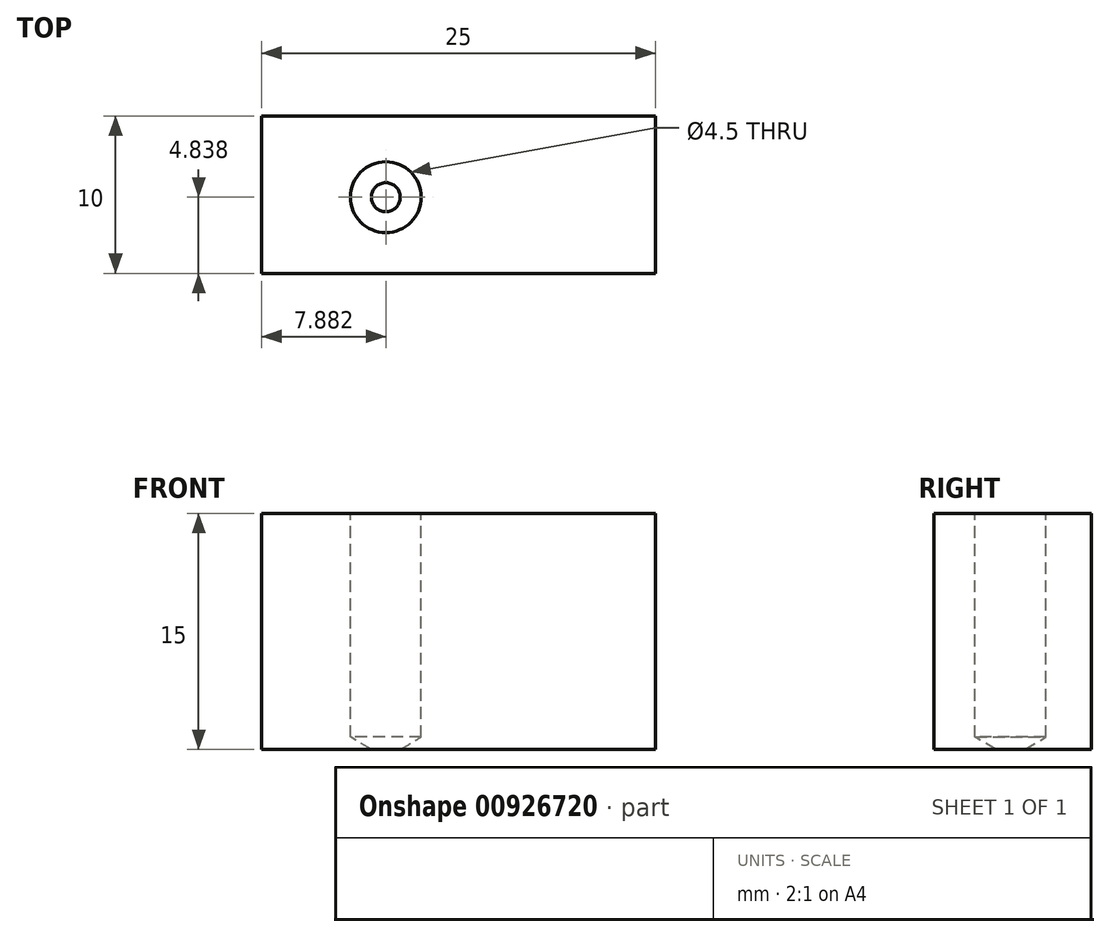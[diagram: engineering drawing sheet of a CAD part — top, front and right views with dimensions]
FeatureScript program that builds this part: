
annotation { "Feature Type Name" : "Feature", "Feature Type Description" : "" }
export const myFeature = defineFeature(function(context is Context, id is Id, definition is map)
    precondition{}
    {
        {
            var Q0;
            Q0=qCreatedBy(makeId("Top.planeOp"),FACE);
            var sketch = newSketch(context, id + "F0", { "sketchPlane" : qUnion([Q0])});
            skLineSegment(sketch, "E0", {"start": v(-46.8, 0.97) * mm, "end": v(-21.8, 0.97) * mm});
            skLineSegment(sketch, "E1", {"start": v(-21.8, 0.97) * mm, "end": v(-21.8, -9.03) * mm});
            skLineSegment(sketch, "E2", {"start": v(-21.8, -9.03) * mm, "end": v(-46.8, -9.03) * mm});
            skLineSegment(sketch, "E3", {"start": v(-46.8, -9.03) * mm, "end": v(-46.8, 0.97) * mm});
            skSolve(sketch);
        }
        {
            var Q0;
            Q0=makeQuery(id+"F0.imprint","IMPRINT",FACE,{"disambiguationData":[TD([[makeQuery(id+"F0.imprint","IMPRINT",EDGE,{"derivedFrom":sQuery(id+"F0.wireOp",EDGE,"E0")}),-1.0]])]});
            extrude(context, id + "F1", {"entities" : qUnion([Q0]), "depth" : 15 * mm, "offsetDistance" : 25.4 * mm});
        }
        {
            var Q0;
            Q0=makeQuery(id+"F1.opExtrude","CAP_FACE",FACE,{"disambiguationData":[OSD([sQuery(id+"F0.wireOp",EDGE,"E0"),sQuery(id+"F0.wireOp",EDGE,"E1"),sQuery(id+"F0.wireOp",EDGE,"E2"),sQuery(id+"F0.wireOp",EDGE,"E3")])],"isStart":false});
            var sketch = newSketch(context, id + "F2", { "sketchPlane" : qUnion([Q0])});
            skPoint(sketch, "E4", {"position": v(-38.92, -4.2) * mm});
            skSolve(sketch);
        }
        {
            var Q0;
            Q0=sQuery(id+"F2.wireOp",VERTEX,"E4");
            var Q1;
            Q1=makeQuery(id+"F1.opExtrude","SWEPT_BODY",BODY,{"disambiguationData":[OSD([sQuery(id+"F0.wireOp",EDGE,"E0"),sQuery(id+"F0.wireOp",EDGE,"E1"),sQuery(id+"F0.wireOp",EDGE,"E2"),sQuery(id+"F0.wireOp",EDGE,"E3")])]});
            hole(context, id + "F3", {"style" : HoleStyle.SIMPLE, "endStyle" : HoleEndStyle.BLIND, "standardTappedOrClearance" : lookupTablePath({ "standard" : "ISO", "engagement" : "75%", "pitch" : "0.5 mm", "size" : "M5", "type" : "Tapped" }), "standardBlindInLast" : lookupTablePath({ "standard" : "ISO", "engagement" : "75%", "pitch" : "0.5 mm", "size" : "M5", "type" : "Tapped" }), "holeDiameter" : 4.5 * mm, "majorDiameter" : 5 * mm, "showTappedDepth" : true, "holeDepth" : 14.2 * mm, "isTappedThrough" : true, "tappedDepth" : 12.7 * mm, "tapClearance" : 3, "locations" : qUnion([Q0]), "scope" : qUnion([Q1])});
        }
    });
